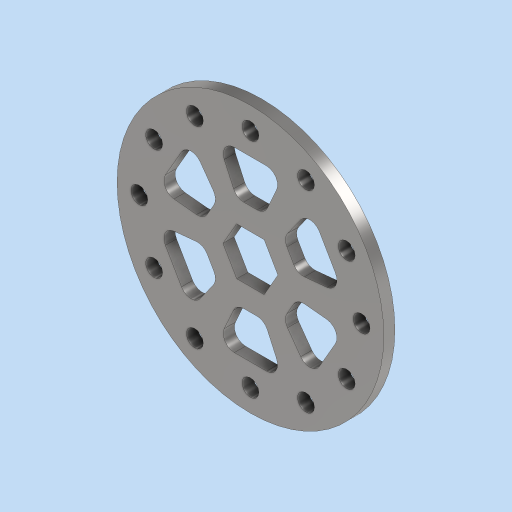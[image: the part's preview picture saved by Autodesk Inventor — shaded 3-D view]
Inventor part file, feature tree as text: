
AUTODESK INVENTOR PART (.ipt)
format: ipt  version: 2023 (Build 270158000, 158)  size: 224,256 bytes
history: native  units: in
note: dims shown in document units (in); Inventor stores cm internally (conversion verified against a paired STEP export)
features: extrude x2, sketch x1, fillet x1, pattern_circular x1
ambient origin geometry x8: Origin, YZ Plane, XZ Plane, XY Plane, X Axis, Y Axis, Z Axis, Center Point
bodies: Solid1 (feature_tree)
feature tree (5):
  sketch  "Sketch1"  dims[d0=3.0in d1=0.5354in d2=2.5in d3=0.19in d4=4.7244in d6=360.0deg d8=0.125in d9=0.0in d10=0.125in d11=0.0in d12=0.125in d13=2.3622in d14=360.0deg d16=0.25in d18=0.3125in d19=0.75in d20=0.5in]
  extrude  "Extrusion1"  Depth=0.5354in
  extrude  "Extrusion2"  Depth=0.25in
  fillet  "Fillet1"  Radius=0.19in
  pattern_circular  "Circular Pattern1"  Count=12 Angle=360.0deg
